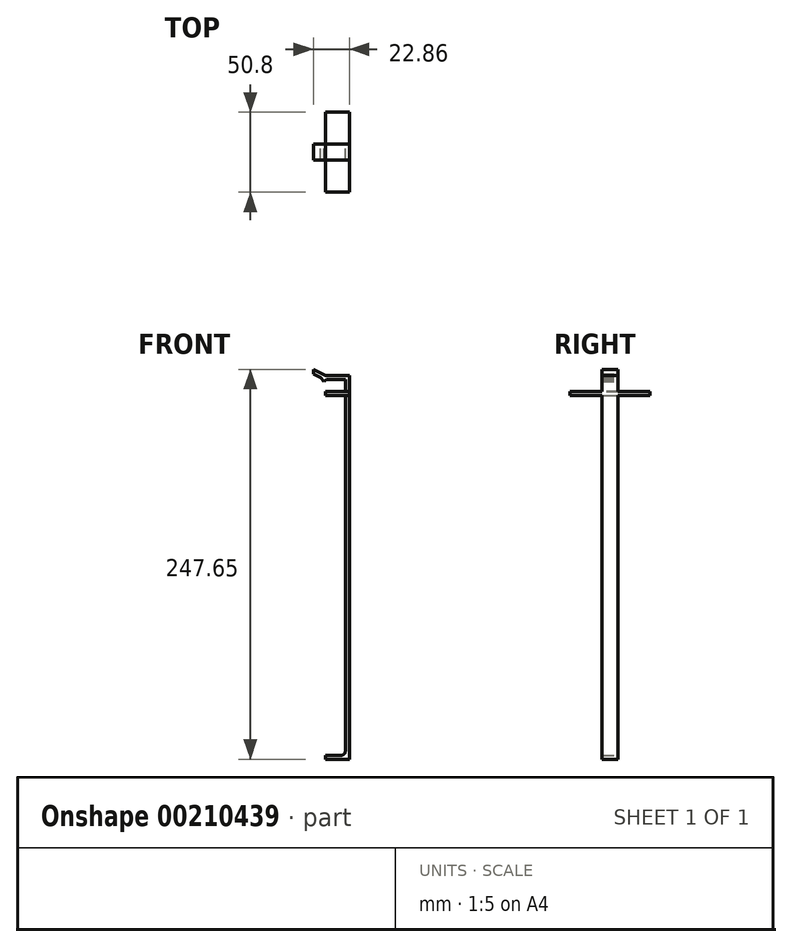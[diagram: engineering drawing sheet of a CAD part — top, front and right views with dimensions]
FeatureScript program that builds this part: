
annotation { "Feature Type Name" : "Feature", "Feature Type Description" : "" }
export const myFeature = defineFeature(function(context is Context, id is Id, definition is map)
    precondition{}
    {
        {
            var Q0;
            Q0=qCreatedBy(makeId("Front.planeOp"),FACE);
            var sketch = newSketch(context, id + "F0", { "sketchPlane" : qUnion([Q0])});
            skLineSegment(sketch, "E0", {"start": v(0, -121.92) * mm, "end": v(0, 121.92) * mm});
            skLineSegment(sketch, "E1", {"start": v(0, 121.92) * mm, "end": v(-15.24, 121.92) * mm});
            skLineSegment(sketch, "E2", {"start": v(-15.24, 121.92) * mm, "end": v(-22.86, 125.73) * mm});
            skLineSegment(sketch, "E3", {"start": v(0, -121.92) * mm, "end": v(-15.24, -121.92) * mm});
            skLineSegment(sketch, "E4.0", {"start": v(-15.84, 119.38) * mm, "end": v(-22.86, 122.9) * mm});
            skLineSegment(sketch, "E4.1", {"start": v(-2.54, 119.38) * mm, "end": v(-15.84, 119.38) * mm});
            skLineSegment(sketch, "E4.2", {"start": v(-2.54, -119.38) * mm, "end": v(-2.54, 119.38) * mm});
            skLineSegment(sketch, "E4.3", {"start": v(-2.54, -119.38) * mm, "end": v(-15.24, -119.38) * mm});
            skLineSegment(sketch, "E5", {"start": v(-22.86, 125.73) * mm, "end": v(-22.86, 122.9) * mm});
            skLineSegment(sketch, "E6", {"start": v(0, 111.76) * mm, "end": v(-15.24, 111.76) * mm});
            skLineSegment(sketch, "E7", {"start": v(-15.24, 111.76) * mm, "end": v(-15.24, 109.22) * mm});
            skLineSegment(sketch, "E8", {"start": v(-15.24, 109.22) * mm, "end": v(0, 109.22) * mm});
            skLineSegment(sketch, "E9", {"start": v(-15.24, -119.38) * mm, "end": v(-15.24, -121.92) * mm});
            skLineSegment(sketch, "E10", {"start": v(-14.3, 119.38) * mm, "end": v(-15.95, 117.91) * mm});
            skLineSegment(sketch, "E11", {"start": v(-15.95, 117.91) * mm, "end": v(-18.4, 120.66) * mm});
            skSolve(sketch);
        }
        {
            var Q0;
            {var subQ5=sQuery(id+"F0.wireOp",EDGE,"E1");Q0=makeQuery(id+"F0.imprint","IMPRINT",FACE,{"disambiguationData":[TD([[makeQuery(id+"F0.imprint","IMPRINT",EDGE,{"derivedFrom":subQ5}),1.0]])]});}
            var Q1;
            {var subQ4=sQuery(id+"F0.wireOp",EDGE,"E3");Q1=makeQuery(id+"F0.imprint","IMPRINT",FACE,{"disambiguationData":[TD([[makeQuery(id+"F0.imprint","IMPRINT",EDGE,{"derivedFrom":subQ4}),-1.0]])]});}
            var Q2;
            {var subQ0=sQuery(id+"F0.wireOp",EDGE,"E6");var subQ1=sQuery(id+"F0.wireOp",EDGE,"E0");var subQ2=makeQuery(id+"F0.imprint","INTERSECT",VERTEX,{"derivedFrom":[subQ1,subQ0]});Q2=makeQuery(id+"F0.imprint","IMPRINT",FACE,{"disambiguationData":[TD([[makeQuery(id+"F0.imprint","IMPRINT",EDGE,{"disambiguationData":[TD([[subQ2,1.0]])],"derivedFrom":subQ1}),1.0]])]});}
            var Q3;
            {var subQ4=sQuery(id+"F0.wireOp",EDGE,"E10");Q3=makeQuery(id+"F0.imprint","IMPRINT",FACE,{"disambiguationData":[TD([[makeQuery(id+"F0.imprint","IMPRINT",EDGE,{"derivedFrom":subQ4}),-1.0]])]});}
            extrude(context, id + "F1", {"entities" : qUnion([Q0, Q1, Q2, Q3]), "depth" : 5.08 * mm, "hasSecondDirection" : true, "secondDirectionOppositeDirection" : true, "secondDirectionDepth" : 5.08 * mm});
        }
        {
            var Q0;
            {var subQ0=sQuery(id+"F0.wireOp",EDGE,"E6");Q0=makeQuery(id+"F0.imprint","IMPRINT",FACE,{"disambiguationData":[TD([[makeQuery(id+"F0.imprint","IMPRINT",EDGE,{"derivedFrom":subQ0}),1.0]])]});}
            extrude(context, id + "F2", {"entities" : qUnion([Q0]), "operationType" : NewBodyOperationType.ADD, "depth" : 25.4 * mm, "hasSecondDirection" : true, "secondDirectionOppositeDirection" : true, "secondDirectionDepth" : 25.4 * mm});
        }
        {
            var Q0;
            Q0=makeQuery(id+"F1.opExtrude","SWEPT_EDGE",EDGE,{"disambiguationData":[OSD([sQuery(id+"F0.wireOp",EDGE,"E4.2"),sQuery(id+"F0.wireOp",EDGE,"E4.3")])]});
            fillet(context, id + "F3", {"entities" : qUnion([Q0]), "radius" : 2.54 * mm, "tangentPropagation" : true, "allowEdgeOverflow" : false});
        }
    });
